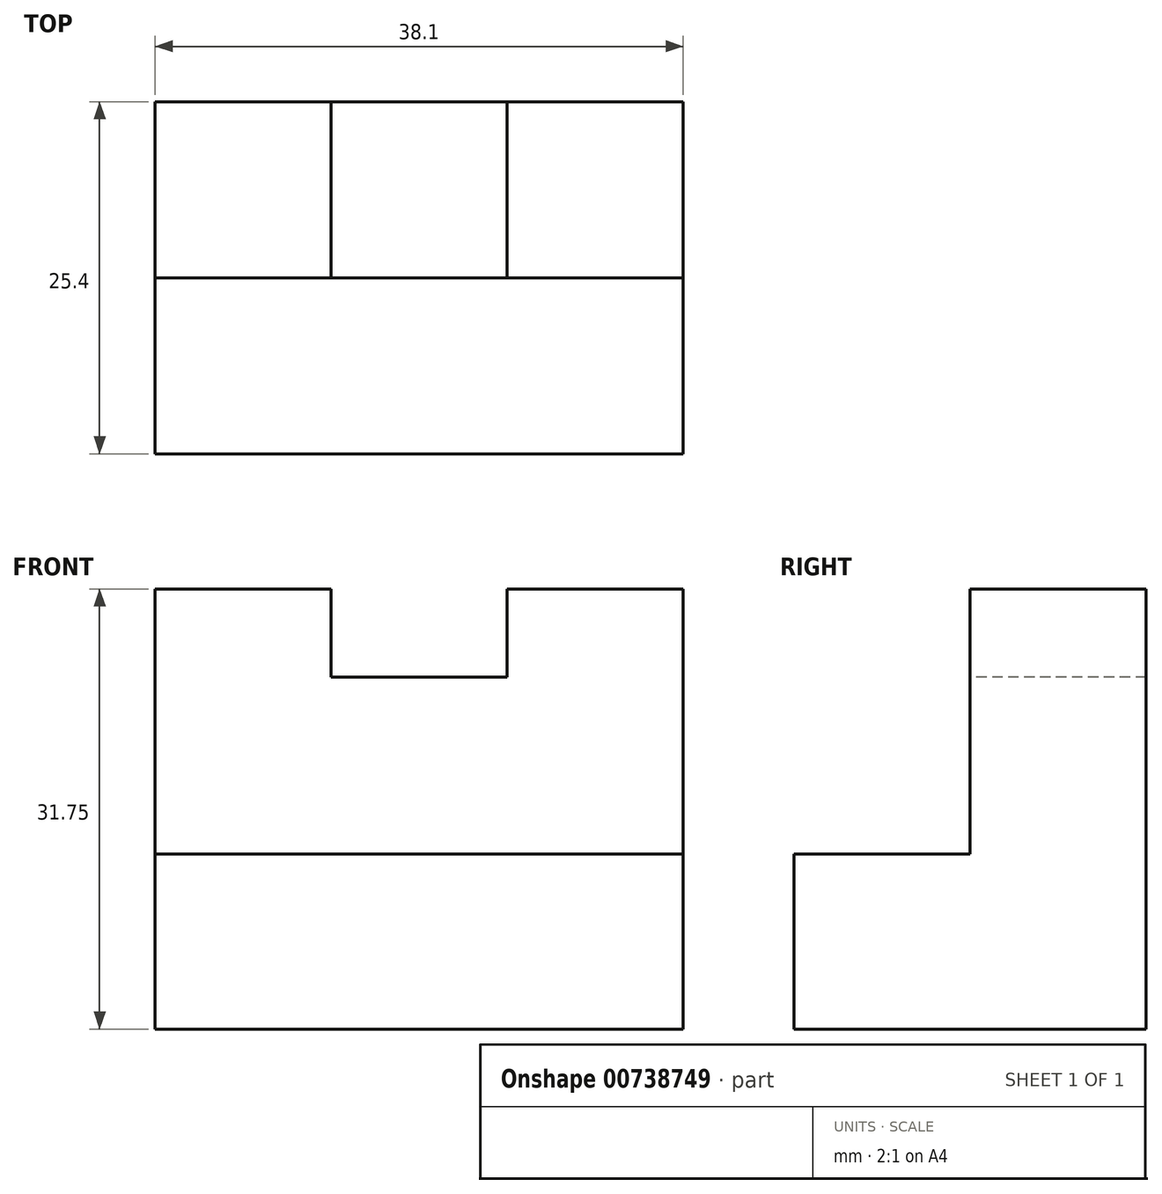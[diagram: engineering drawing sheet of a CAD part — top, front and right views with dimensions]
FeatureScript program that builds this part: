
annotation { "Feature Type Name" : "Feature", "Feature Type Description" : "" }
export const myFeature = defineFeature(function(context is Context, id is Id, definition is map)
    precondition{}
    {
        {
            var Q0;
            Q0=qCreatedBy(makeId("Front.planeOp"),FACE);
            var sketch = newSketch(context, id + "F0", { "sketchPlane" : qUnion([Q0])});
            skLineSegment(sketch, "E0", {"start": v(0, 0) * mm, "end": v(38.1, 0) * mm});
            skLineSegment(sketch, "E1", {"start": v(38.1, 0) * mm, "end": v(38.1, 31.75) * mm});
            skLineSegment(sketch, "E2", {"start": v(38.1, 31.75) * mm, "end": v(0, 31.75) * mm});
            skLineSegment(sketch, "E3", {"start": v(0, 0) * mm, "end": v(0, 31.75) * mm});
            skSolve(sketch);
        }
        {
            var Q0;
            Q0 = qSketchRegion(id + "F0", true);
            extrude(context, id + "F1", {"entities" : qUnion([Q0]), "depth" : 25.4 * mm, "offsetDistance" : 25.4 * mm});
        }
        {
            var Q0;
            Q0=makeQuery(id+"F1.opExtrude","SWEPT_FACE",FACE,{"disambiguationData":[OSD([sQuery(id+"F0.wireOp",EDGE,"E1")])]});
            var sketch = newSketch(context, id + "F2", { "sketchPlane" : qUnion([Q0])});
            skLineSegment(sketch, "E4", {"start": v(-12.7, 31.75) * mm, "end": v(-12.7, 12.63) * mm});
            skLineSegment(sketch, "E5", {"start": v(-12.7, 12.63) * mm, "end": v(-25.4, 12.63) * mm});
            skSolve(sketch);
        }
        {
            var Q0;
            {var subQ0=sQuery(id+"F2.wireOp",EDGE,"E4");Q0=makeQuery(id+"F2.imprint","IMPRINT",FACE,{"disambiguationData":[TD([[makeQuery(id+"F2.imprint","IMPRINT",EDGE,{"derivedFrom":subQ0}),-1.0]])]});}
            extrude(context, id + "F3", {"entities" : qUnion([Q0]), "operationType" : NewBodyOperationType.REMOVE, "endBound" : BoundingType.THROUGH_ALL, "oppositeDirection" : true, "depth" : 25.4 * mm, "offsetDistance" : 25.4 * mm});
        }
        {
            var Q0;
            Q0=makeQuery(id+"F3.boolean.opBoolean","COPY",FACE,{"derivedFrom":makeQuery(id+"F3.opExtrude","SWEPT_FACE",FACE,{"disambiguationData":[OSD([sQuery(id+"F2.wireOp",EDGE,"E4")])]})});
            var sketch = newSketch(context, id + "F4", { "sketchPlane" : qUnion([Q0])});
            skLineSegment(sketch, "E6", {"start": v(12.7, 31.75) * mm, "end": v(12.7, 25.4) * mm});
            skLineSegment(sketch, "E7", {"start": v(12.7, 25.4) * mm, "end": v(25.4, 25.4) * mm});
            skLineSegment(sketch, "E8", {"start": v(25.4, 25.4) * mm, "end": v(25.4, 31.75) * mm});
            skSolve(sketch);
        }
        {
            var Q0;
            {var subQ0=sQuery(id+"F4.wireOp",EDGE,"E6");Q0=makeQuery(id+"F4.imprint","IMPRINT",FACE,{"disambiguationData":[TD([[makeQuery(id+"F4.imprint","IMPRINT",EDGE,{"derivedFrom":subQ0}),1.0]])]});}
            extrude(context, id + "F5", {"entities" : qUnion([Q0]), "operationType" : NewBodyOperationType.REMOVE, "endBound" : BoundingType.THROUGH_ALL, "oppositeDirection" : true, "depth" : 25.4 * mm, "offsetDistance" : 25.4 * mm});
        }
    });
